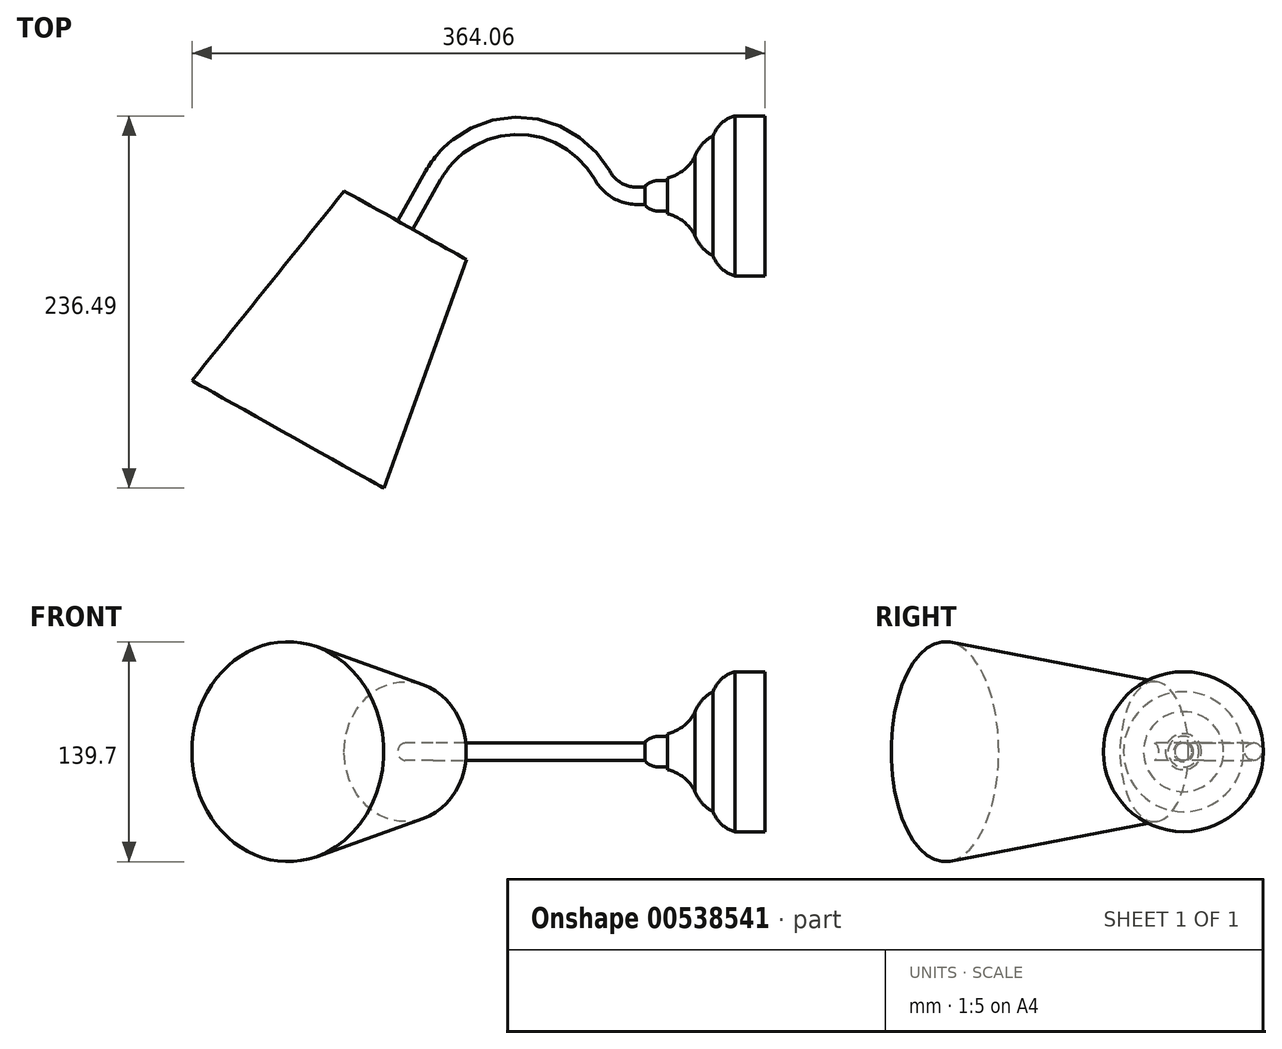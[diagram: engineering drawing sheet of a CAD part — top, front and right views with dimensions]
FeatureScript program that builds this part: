
annotation { "Feature Type Name" : "Feature", "Feature Type Description" : "" }
export const myFeature = defineFeature(function(context is Context, id is Id, definition is map)
    precondition{}
    {
        {
            var Q0;
            Q0=qCreatedBy(makeId("Top.planeOp"),FACE);
            var sketch = newSketch(context, id + "F0", { "sketchPlane" : qUnion([Q0])});
            skLineSegment(sketch, "E0", {"start": v(0, 0) * mm, "end": v(-76.2, 0) * mm});
            skLineSegment(sketch, "E1", {"start": v(0, 0) * mm, "end": v(0, 50.8) * mm});
            skLineSegment(sketch, "E2", {"start": v(0, 50.8) * mm, "end": v(-19.05, 50.8) * mm});
            skArc(sketch, "E3", {"start": v(-19.05, 50.8) * mm, "mid": v(-27.65, 46.22) * mm, "end": v(-33.02, 38.1) * mm});
            skArc(sketch, "E4", {"start": v(-33.02, 38.1) * mm, "mid": v(-39.95, 32.85) * mm, "end": v(-44.45, 25.4) * mm});
            skArc(sketch, "E5", {"start": v(-62.18, 11.43) * mm, "mid": v(-51.75, 16.43) * mm, "end": v(-44.45, 25.4) * mm});
            skLineSegment(sketch, "E6", {"start": v(-62.18, 11.43) * mm, "end": v(-62.18, 9.8) * mm});
            skLineSegment(sketch, "E7", {"start": v(-62.18, 9.8) * mm, "end": v(-66.9, 9.8) * mm});
            skArc(sketch, "E8", {"start": v(-66.9, 9.8) * mm, "mid": v(-71.86, 8.9) * mm, "end": v(-76.2, 6.35) * mm});
            skLineSegment(sketch, "E9", {"start": v(-76.2, 0) * mm, "end": v(-76.2, 6.35) * mm});
            skSolve(sketch);
        }
        {
            var Q0;
            Q0=makeQuery(id+"F0.imprint","IMPRINT",FACE,{"disambiguationData":[TD([[makeQuery(id+"F0.imprint","IMPRINT",EDGE,{"derivedFrom":sQuery(id+"F0.wireOp",EDGE,"E0")}),-1.0]])]});
            var Q1;
            Q1=sQuery(id+"F0.wireOp",EDGE,"E0");
            revolve(context, id + "F1", {"entities" : qUnion([Q0]), "axis" : qUnion([Q1]), "revolveType" : RevolveType.FULL});
        }
        {
            var Q0;
            Q0=qCreatedBy(makeId("Top.planeOp"),FACE);
            var sketch = newSketch(context, id + "F2", { "sketchPlane" : qUnion([Q0])});
            skLineSegment(sketch, "E10", {"start": v(-76.2, 0) * mm, "end": v(-81.28, 0) * mm});
            skArc(sketch, "E11", {"start": v(-103.43, 12.98) * mm, "mid": v(-94.12, 3.48) * mm, "end": v(-81.28, 0) * mm});
            skArc(sketch, "E12", {"start": v(-103.43, 12.98) * mm, "mid": v(-157.16, 44.45) * mm, "end": v(-210.9, 12.98) * mm});
            skLineSegment(sketch, "E13", {"start": v(-210.9, 12.98) * mm, "end": v(-228.6, -18.6) * mm});
            skLineSegment(sketch, "E14", {"start": v(-157.16, 44.45) * mm, "end": v(-233.69, 44.45) * mm, "construction": true});
            skPoint(sketch, "E14.endSnap0", {"position": v(-157.16, 44.45) * mm});
            skSolve(sketch);
        }
        {
            var Q0;
            Q0=makeQuery(id+"F1.opRevolve","SWEPT_FACE",FACE,{"disambiguationData":[OSD([sQuery(id+"F0.wireOp",EDGE,"E9")])]});
            var sketch = newSketch(context, id + "F3", { "sketchPlane" : qUnion([Q0])});
            skCircle(sketch, "E15", {"center": v(0, 0) * mm, "radius": 5.45 * mm});
            skSolve(sketch);
        }
        {
            var Q0;
            Q0 = qSketchRegion(id + "F3", true);
            var Q1;
            Q1 = qConstructionFilter(qBodyType(qCreatedBy(id + "F2" ,EDGE), BodyType.WIRE), ConstructionObject.NO);
            sweep(context, id + "F4", {"operationType" : NewBodyOperationType.ADD, "profiles" : qUnion([Q0]), "path" : qUnion([Q1])});
        }
        {
            var Q0;
            Q0=qCreatedBy(makeId("Top.planeOp"),FACE);
            var sketch = newSketch(context, id + "F5", { "sketchPlane" : qUnion([Q0])});
            skLineSegment(sketch, "E16", {"start": v(-223.85, -21.27) * mm, "end": v(-206.14, 10.31) * mm, "construction": true});
            skLineSegment(sketch, "E17", {"start": v(-215.65, 15.64) * mm, "end": v(-233.35, -15.94) * mm, "construction": true});
            skLineSegment(sketch, "E18", {"start": v(-233.35, -15.94) * mm, "end": v(-223.85, -21.27) * mm, "construction": true});
            skLineSegment(sketch, "E19", {"start": v(-228.6, -18.6) * mm, "end": v(-303.13, -151.53) * mm});
            skLineSegment(sketch, "E20", {"start": v(-228.6, -18.6) * mm, "end": v(-189.83, -40.34) * mm});
            skLineSegment(sketch, "E21", {"start": v(-303.13, -151.53) * mm, "end": v(-242.2, -185.7) * mm});
            skLineSegment(sketch, "E22", {"start": v(-242.2, -185.7) * mm, "end": v(-189.83, -40.34) * mm});
            skSolve(sketch);
        }
        {
            var Q0;
            Q0=makeQuery(id+"F5.imprint","IMPRINT",FACE,{"disambiguationData":[TD([[makeQuery(id+"F5.imprint","IMPRINT",EDGE,{"derivedFrom":sQuery(id+"F5.wireOp",EDGE,"E19")}),1.0]])]});
            var Q1;
            Q1=sQuery(id+"F5.wireOp",EDGE,"E19");
            revolve(context, id + "F6", {"operationType" : NewBodyOperationType.ADD, "entities" : qUnion([Q0]), "axis" : qUnion([Q1]), "revolveType" : RevolveType.FULL});
        }
    });
